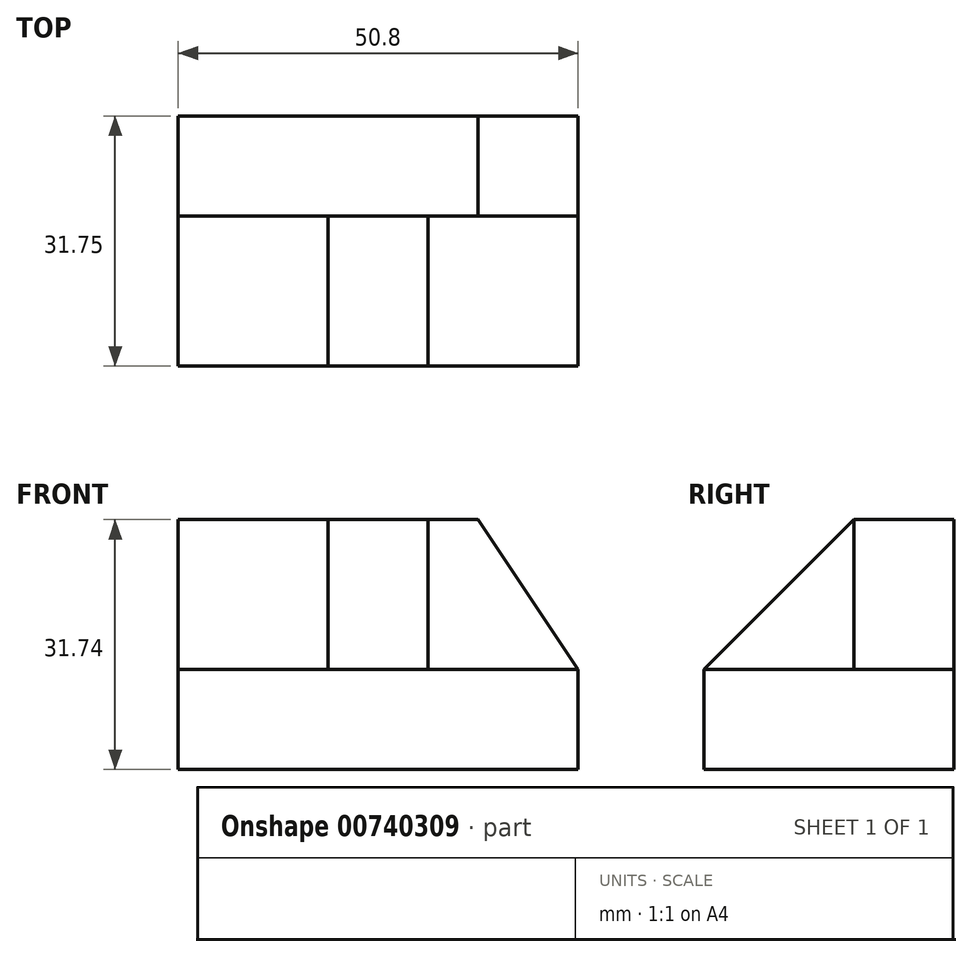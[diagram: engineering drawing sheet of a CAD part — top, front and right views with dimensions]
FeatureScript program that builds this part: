
annotation { "Feature Type Name" : "Feature", "Feature Type Description" : "" }
export const myFeature = defineFeature(function(context is Context, id is Id, definition is map)
    precondition{}
    {
        {
            var Q0;
            Q0=qCreatedBy(makeId("Front.planeOp"),FACE);
            var sketch = newSketch(context, id + "F0", { "sketchPlane" : qUnion([Q0])});
            skLineSegment(sketch, "E0", {"start": v(0, 0) * mm, "end": v(50.8, 0) * mm});
            skLineSegment(sketch, "E1", {"start": v(50.8, 0) * mm, "end": v(50.8, 31.74) * mm});
            skLineSegment(sketch, "E2", {"start": v(50.8, 31.74) * mm, "end": v(0, 31.74) * mm});
            skLineSegment(sketch, "E3", {"start": v(0, 31.74) * mm, "end": v(0, 0) * mm});
            skSolve(sketch);
        }
        {
            var Q0;
            Q0 = qSketchRegion(id + "F0", true);
            extrude(context, id + "F1", {"entities" : qUnion([Q0]), "depth" : 31.75 * mm, "offsetDistance" : 25.4 * mm});
        }
        {
            var Q0;
            Q0=makeQuery(id+"F1.opExtrude","CAP_FACE",FACE,{"disambiguationData":[OSD([sQuery(id+"F0.wireOp",EDGE,"E0"),sQuery(id+"F0.wireOp",EDGE,"E1"),sQuery(id+"F0.wireOp",EDGE,"E2"),sQuery(id+"F0.wireOp",EDGE,"E3")])],"isStart":false});
            var sketch = newSketch(context, id + "F2", { "sketchPlane" : qUnion([Q0])});
            skLineSegment(sketch, "E4", {"start": v(50.8, 0) * mm, "end": v(50.8, 12.7) * mm});
            skLineSegment(sketch, "E5", {"start": v(0, 31.74) * mm, "end": v(38.1, 31.74) * mm});
            skLineSegment(sketch, "E6", {"start": v(38.1, 31.74) * mm, "end": v(50.8, 12.7) * mm});
            skLineSegment(sketch, "E7", {"start": v(50.8, 12.7) * mm, "end": v(50.8, 31.74) * mm});
            skLineSegment(sketch, "E8", {"start": v(50.8, 31.74) * mm, "end": v(38.1, 31.74) * mm});
            skSolve(sketch);
        }
        {
            var Q0;
            Q0 = qSketchRegion(id + "F2", true);
            extrude(context, id + "F3", {"entities" : qUnion([Q0]), "operationType" : NewBodyOperationType.REMOVE, "endBound" : BoundingType.THROUGH_ALL, "oppositeDirection" : true, "depth" : 25.4 * mm, "offsetDistance" : 25.4 * mm});
        }
        {
            var Q0;
            Q0=makeQuery(id+"F1.opExtrude","CAP_FACE",FACE,{"disambiguationData":[OSD([sQuery(id+"F0.wireOp",EDGE,"E0"),sQuery(id+"F0.wireOp",EDGE,"E1"),sQuery(id+"F0.wireOp",EDGE,"E2"),sQuery(id+"F0.wireOp",EDGE,"E3")])],"isStart":false});
            var sketch = newSketch(context, id + "F4", { "sketchPlane" : qUnion([Q0])});
            skLineSegment(sketch, "E9", {"start": v(50.8, 12.7) * mm, "end": v(31.74, 12.7) * mm});
            skLineSegment(sketch, "E10", {"start": v(31.74, 12.7) * mm, "end": v(31.74, 31.74) * mm});
            skLineSegment(sketch, "E11", {"start": v(31.74, 31.74) * mm, "end": v(38.1, 31.74) * mm});
            skLineSegment(sketch, "E12", {"start": v(38.1, 31.74) * mm, "end": v(50.8, 12.7) * mm});
            skSolve(sketch);
        }
        {
            var Q0;
            Q0=makeQuery(id+"F4.imprint","IMPRINT",FACE,{"disambiguationData":[TD([[makeQuery(id+"F4.imprint","IMPRINT",EDGE,{"derivedFrom":sQuery(id+"F4.wireOp",EDGE,"E9")}),-1.0]])]});
            extrude(context, id + "F5", {"entities" : qUnion([Q0]), "operationType" : NewBodyOperationType.REMOVE, "oppositeDirection" : true, "depth" : 19.05 * mm, "offsetDistance" : 25.4 * mm});
        }
        {
            var Q0;
            Q0=makeQuery(id+"F5.boolean.opBoolean","COPY",FACE,{"derivedFrom":makeQuery(id+"F5.opExtrude","SWEPT_FACE",FACE,{"disambiguationData":[OSD([sQuery(id+"F4.wireOp",EDGE,"E10")])]})});
            var sketch = newSketch(context, id + "F6", { "sketchPlane" : qUnion([Q0])});
            skLineSegment(sketch, "E13", {"start": v(-12.7, 31.74) * mm, "end": v(-31.75, 12.7) * mm});
            skSolve(sketch);
        }
        {
            var Q0;
            Q0 = qSketchRegion(id + "F6", true);
            var Q1;
            Q1=makeQuery(id+"F6.imprint","IMPRINT",FACE,{"disambiguationData":[TD([[makeQuery(id+"F6.imprint","IMPRINT",EDGE,{"derivedFrom":sQuery(id+"F6.wireOp",EDGE,"E13")}),-1.0]])]});
            extrude(context, id + "F7", {"entities" : qUnion([Q0, Q1]), "operationType" : NewBodyOperationType.REMOVE, "endBound" : BoundingType.THROUGH_ALL, "oppositeDirection" : true, "depth" : 25.4 * mm, "offsetDistance" : 25.4 * mm});
        }
        {
            var Q0;
            Q0=makeQuery(id+"F1.opExtrude","SWEPT_FACE",FACE,{"disambiguationData":[OSD([sQuery(id+"F0.wireOp",EDGE,"E3")])]});
            var sketch = newSketch(context, id + "F8", { "sketchPlane" : qUnion([Q0])});
            skLineSegment(sketch, "E14", {"start": v(31.75, 12.7) * mm, "end": v(12.7, 12.7) * mm});
            skLineSegment(sketch, "E15", {"start": v(12.7, 12.7) * mm, "end": v(12.7, 31.74) * mm});
            skSolve(sketch);
        }
        {
            var Q0;
            Q0 = qSketchRegion(id + "F8", true);
            var Q1;
            Q1=makeQuery(id+"F8.imprint","IMPRINT",FACE,{"disambiguationData":[TD([[makeQuery(id+"F8.imprint","IMPRINT",EDGE,{"derivedFrom":sQuery(id+"F8.wireOp",EDGE,"E14")}),-1.0]])]});
            extrude(context, id + "F9", {"entities" : qUnion([Q0, Q1]), "operationType" : NewBodyOperationType.REMOVE, "oppositeDirection" : true, "depth" : 19.05 * mm, "offsetDistance" : 25.4 * mm});
        }
    });
